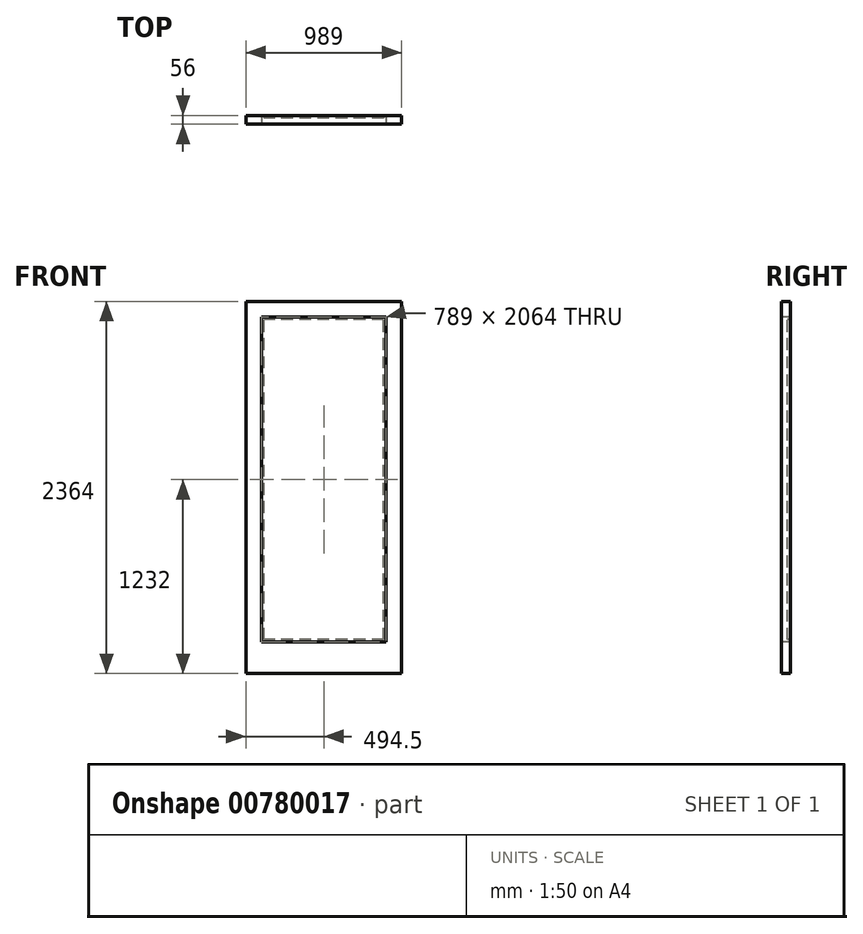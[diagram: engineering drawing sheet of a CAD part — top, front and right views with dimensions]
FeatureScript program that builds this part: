
annotation { "Feature Type Name" : "Feature", "Feature Type Description" : "" }
export const myFeature = defineFeature(function(context is Context, id is Id, definition is map)
    precondition{}
    {
        {
            var Q0;
            Q0=qCreatedBy(makeId("Front.planeOp"),FACE);
            var sketch = newSketch(context, id + "F0", { "sketchPlane" : qUnion([Q0])});
            skLineSegment(sketch, "E0.bottom", {"start": v(494.5, -1182) * mm, "end": v(-494.5, -1182) * mm});
            skLineSegment(sketch, "E0.top", {"start": v(494.5, 1182) * mm, "end": v(-494.5, 1182) * mm});
            skLineSegment(sketch, "E0.left", {"start": v(494.5, -1182) * mm, "end": v(494.5, 1182) * mm});
            skLineSegment(sketch, "E0.right", {"start": v(-494.5, -1182) * mm, "end": v(-494.5, 1182) * mm});
            skPoint(sketch, "E0.middle", {"position": v(0, 0) * mm});
            skLineSegment(sketch, "E1.0", {"start": v(-394.5, -982) * mm, "end": v(-394.5, 1082) * mm});
            skLineSegment(sketch, "E1.1", {"start": v(394.5, 1082) * mm, "end": v(-394.5, 1082) * mm});
            skLineSegment(sketch, "E1.2", {"start": v(394.5, -982) * mm, "end": v(394.5, 1082) * mm});
            skLineSegment(sketch, "E2.0", {"start": v(394.5, -982) * mm, "end": v(-394.5, -982) * mm});
            skSolve(sketch);
        }
        {
            var Q0;
            Q0=makeQuery(id+"F0.imprint","IMPRINT",FACE,{"disambiguationData":[TD([[makeQuery(id+"F0.imprint","IMPRINT",EDGE,{"derivedFrom":sQuery(id+"F0.wireOp",EDGE,"E0.bottom")}),-1.0]])]});
            extrude(context, id + "F1", {"entities" : qUnion([Q0]), "depth" : 56 * mm, "offsetDistance" : 25 * mm});
        }
        {
            var Q0;
            Q0=makeQuery(id+"F1.opExtrude","CAP_FACE",FACE,{"disambiguationData":[OSD([sQuery(id+"F0.wireOp",EDGE,"E0.bottom"),sQuery(id+"F0.wireOp",EDGE,"E0.top"),sQuery(id+"F0.wireOp",EDGE,"E0.left"),sQuery(id+"F0.wireOp",EDGE,"E0.right"),sQuery(id+"F0.wireOp",EDGE,"E1.0"),sQuery(id+"F0.wireOp",EDGE,"E1.1"),sQuery(id+"F0.wireOp",EDGE,"E1.2"),sQuery(id+"F0.wireOp",EDGE,"E2.0")])],"isStart":false});
            var sketch = newSketch(context, id + "F2", { "sketchPlane" : qUnion([Q0])});
            skLineSegment(sketch, "E3.0", {"start": v(379.5, 1067) * mm, "end": v(-379.5, 1067) * mm});
            skLineSegment(sketch, "E3.1", {"start": v(379.5, -967) * mm, "end": v(379.5, 1067) * mm});
            skLineSegment(sketch, "E3.2", {"start": v(379.5, -967) * mm, "end": v(-379.5, -967) * mm});
            skLineSegment(sketch, "E3.3", {"start": v(-379.5, -967) * mm, "end": v(-379.5, 1067) * mm});
            skSolve(sketch);
        }
        {
            var Q0;
            Q0=makeQuery(id+"F2.imprint","IMPRINT",FACE,{"disambiguationData":[TD([[makeQuery(id+"F2.imprint","IMPRINT",EDGE,{"derivedFrom":sQuery(id+"F2.wireOp",EDGE,"E3.0")}),-1.0]])]});
            extrude(context, id + "F3", {"entities" : qUnion([Q0]), "oppositeDirection" : true, "depth" : 56 * mm, "offsetDistance" : 25 * mm});
        }
        {
            var Q0;
            Q0=makeQuery(id+"F3.opExtrude","CAP_FACE",FACE,{"disambiguationData":[OSD([sQuery(id+"F0.wireOp",EDGE,"E1.0"),sQuery(id+"F0.wireOp",EDGE,"E1.1"),sQuery(id+"F0.wireOp",EDGE,"E1.2"),sQuery(id+"F0.wireOp",EDGE,"E2.0"),sQuery(id+"F2.wireOp",EDGE,"E3.0"),sQuery(id+"F2.wireOp",EDGE,"E3.1"),sQuery(id+"F2.wireOp",EDGE,"E3.2"),sQuery(id+"F2.wireOp",EDGE,"E3.3")])],"isStart":true});
            var sketch = newSketch(context, id + "F4", { "sketchPlane" : qUnion([Q0])});
            skLineSegment(sketch, "E4.bottom", {"start": v(-379.5, -967) * mm, "end": v(379.5, -967) * mm});
            skLineSegment(sketch, "E4.top", {"start": v(-379.5, 1067) * mm, "end": v(379.5, 1067) * mm});
            skLineSegment(sketch, "E4.left", {"start": v(-379.5, -967) * mm, "end": v(-379.5, 1067) * mm});
            skLineSegment(sketch, "E4.right", {"start": v(379.5, -967) * mm, "end": v(379.5, 1067) * mm});
            skSolve(sketch);
        }
        {
            var Q0;
            Q0=makeQuery(id+"F4.imprint","IMPRINT",FACE,{"disambiguationData":[TD([[makeQuery(id+"F4.imprint","IMPRINT",EDGE,{"derivedFrom":sQuery(id+"F4.wireOp",EDGE,"E4.bottom")}),-1.0]])]});
            extrude(context, id + "F5", {"entities" : qUnion([Q0]), "operationType" : NewBodyOperationType.ADD, "oppositeDirection" : true, "depth" : 38 * mm, "offsetDistance" : 25 * mm});
        }
    });
